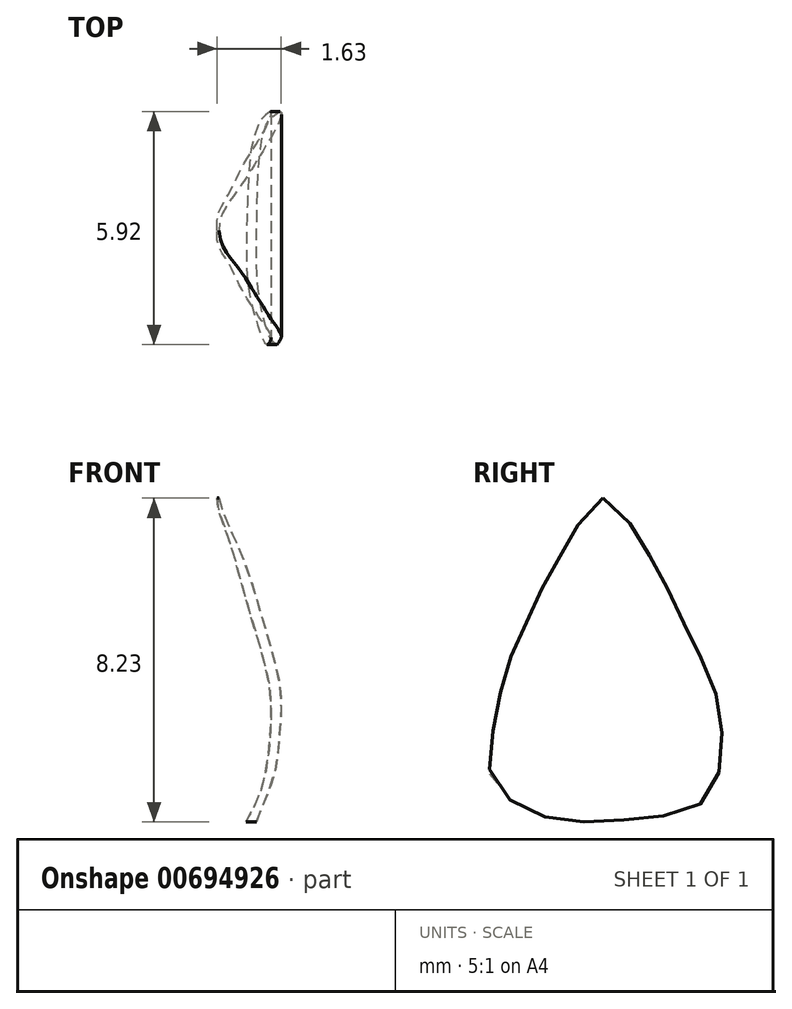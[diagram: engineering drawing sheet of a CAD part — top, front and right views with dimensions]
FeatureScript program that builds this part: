
annotation { "Feature Type Name" : "Feature", "Feature Type Description" : "" }
export const myFeature = defineFeature(function(context is Context, id is Id, definition is map)
    precondition{}
    {
        {
            var Q0;
            Q0=qCreatedBy(makeId("Right.planeOp"),FACE);
            var sketch = newSketch(context, id + "F0", { "sketchPlane" : qUnion([Q0])});
            skPoint(sketch, "E0", {"position": v(0, 0) * mm});
            skFitSpline(sketch, "E1", {"points": [v(0, 5.23) * mm, v(0.74, 4.49) * mm, v(1.52, 3.16) * mm, v(2.08, 2) * mm, v(2.94, 0) * mm, v(2.98, -1.36) * mm, v(2.54, -2.5) * mm, v(0, -2.97) * mm, v(-1.36, -2.9) * mm, v(-2.74, -2.08) * mm, v(-2.84, -1.02) * mm, v(-2.44, 0.9) * mm, v(-1.92, 2.12) * mm, v(-1.48, 3.06) * mm, v(-0.9, 4.09) * mm, v(0, 5.23) * mm]});
            skSolve(sketch);
        }
        {
            var Q0;
            Q0=makeQuery(id+"F0.imprint","IMPRINT",FACE,{"disambiguationData":[TD([[makeQuery(id+"F0.imprint","IMPRINT",EDGE,{"derivedFrom":sQuery(id+"F0.wireOp",EDGE,"E1")}),-1.0]])]});
            extrude(context, id + "F1", {"entities" : qUnion([Q0]), "oppositeDirection" : true, "depth" : 2 * mm, "offsetDistance" : 25 * mm});
        }
        {
            var Q0;
            Q0=qCreatedBy(makeId("Front.planeOp"),FACE);
            var sketch = newSketch(context, id + "F2", { "sketchPlane" : qUnion([Q0])});
            skFitSpline(sketch, "E2", {"points": [v(-1.02, -3.2) * mm, v(-0.6, -2.1) * mm, v(-0.45, -1.52) * mm, v(-0.37, -0.8) * mm, v(-0.33, -0.3) * mm, v(-0.37, 0.51) * mm, v(-0.57, 1.36) * mm, v(-0.88, 2.42) * mm, v(-1.27, 3.62) * mm, v(-1.79, 4.85) * mm, v(-1.96, 5.6) * mm, v(-1.79, 5.7) * mm, v(1.47, 5.16) * mm, v(0.82, -3.57) * mm, v(-0.9, -3.74) * mm, v(-1.02, -3.2) * mm]});
            skFitSpline(sketch, "E3", {"points": [v(-2.01, 5.34) * mm, v(-1.96, 5.08) * mm, v(-1.74, 4.41) * mm, v(-1.42, 3.36) * mm, v(-1.15, 2.4) * mm, v(-0.81, 1.27) * mm, v(-0.62, 0.34) * mm, v(-0.61, -0.9) * mm, v(-0.84, -2.2) * mm, v(-1.18, -2.92) * mm, v(-1.79, -3.56) * mm, v(-4.55, 3.76) * mm, v(-3.45, 5.05) * mm, v(-2.01, 5.34) * mm]});
            skSolve(sketch);
        }
        {
            var Q0;
            Q0=qSketchRegion(id+"F2",true);
            extrude(context, id + "F3", {"entities" : qUnion([Q0]), "operationType" : NewBodyOperationType.REMOVE, "oppositeDirection" : true, "depth" : 8 * mm, "offsetDistance" : 25 * mm, "symmetric" : true});
        }
        {
            var Q0;
            Q0=makeQuery(id+"F1.opExtrude","SWEPT_BODY",BODY,{"disambiguationData":[OSD([sQuery(id+"F0.wireOp",EDGE,"E1")])]});
            transform(context, id + "F4", {"entities" : qUnion([Q0]), "transformType" : TransformType.TRANSLATION_3D, "dx" : 0 * mm, "dy" : 0 * mm, "dz" : 0 * mm, "makeCopy" : true});
        }
    });
